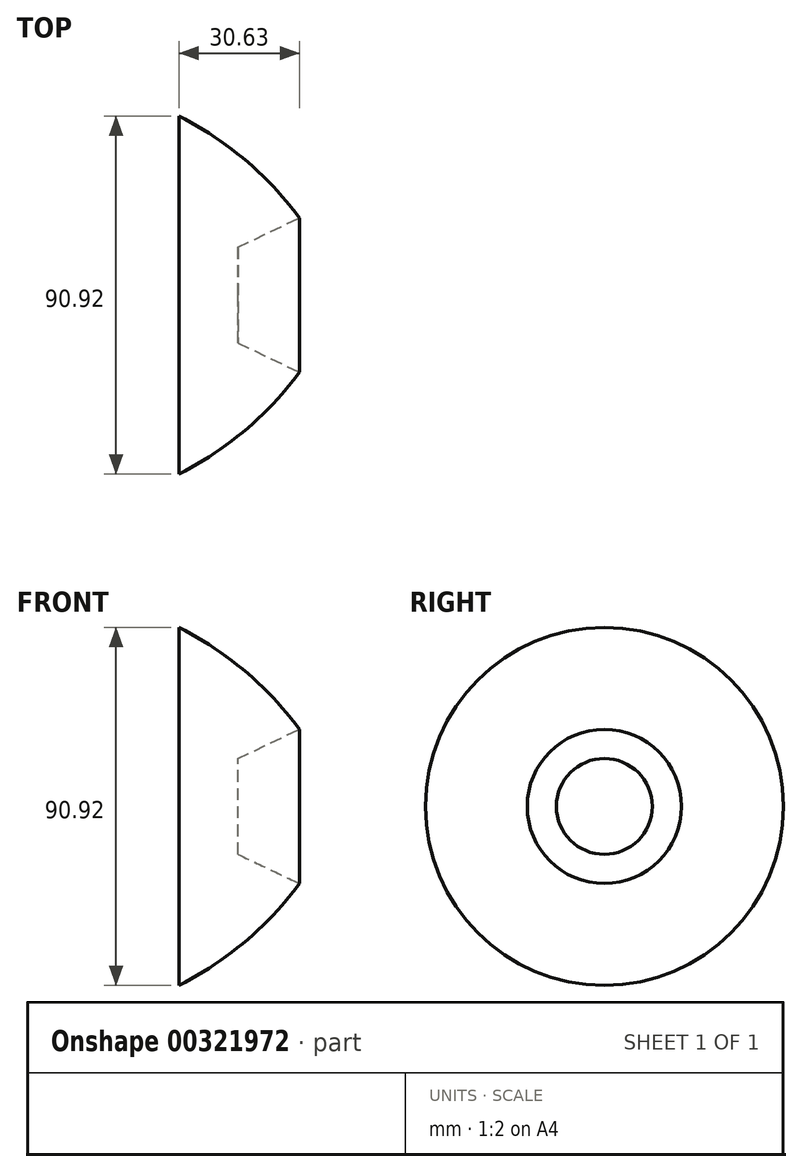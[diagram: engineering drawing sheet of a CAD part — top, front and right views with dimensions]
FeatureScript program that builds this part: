
annotation { "Feature Type Name" : "Feature", "Feature Type Description" : "" }
export const myFeature = defineFeature(function(context is Context, id is Id, definition is map)
    precondition{}
    {
        {
            var Q0;
            Q0=qCreatedBy(makeId("Front.planeOp"),FACE);
            var sketch = newSketch(context, id + "F0", { "sketchPlane" : qUnion([Q0])});
            skLineSegment(sketch, "E0", {"start": v(-23.59, 0) * mm, "end": v(-23.59, 45.46) * mm});
            skLineSegment(sketch, "E1", {"start": v(0, 0) * mm, "end": v(-65.82, 0) * mm, "construction": true});
            skArc(sketch, "E2", {"start": v(7.04, 19.6) * mm, "mid": v(-6.76, 34.33) * mm, "end": v(-23.59, 45.46) * mm});
            skLineSegment(sketch, "E3", {"start": v(7.04, 19.6) * mm, "end": v(-8.56, 12.17) * mm});
            skLineSegment(sketch, "E4", {"start": v(-8.56, 12.17) * mm, "end": v(-8.56, 0) * mm});
            skLineSegment(sketch, "E5", {"start": v(-23.59, 0) * mm, "end": v(-8.56, 0) * mm});
            skSolve(sketch);
        }
        {
            var Q0;
            Q0 = qSketchRegion(id + "F0", true);
            var Q1;
            Q1=sQuery(id+"F0.wireOp",EDGE,"E1");
            revolve(context, id + "F1", {"entities" : qUnion([Q0]), "axis" : qUnion([Q1]), "revolveType" : RevolveType.FULL});
        }
    });
